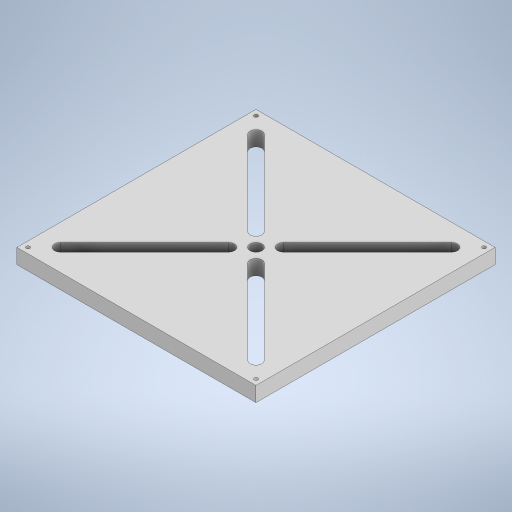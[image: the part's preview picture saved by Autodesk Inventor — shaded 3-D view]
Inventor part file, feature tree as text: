
AUTODESK INVENTOR PART (.ipt)
format: ipt  version: 2023 (Build 270158000, 158)  size: 280,576 bytes
history: native  units: in
note: dims shown in document units (in); Inventor stores cm internally (conversion verified against a paired STEP export)
features: sketch x3, extrude x2, projected_geometry x2
ambient origin geometry x8: Origin, YZ Plane, XZ Plane, XY Plane, X Axis, Y Axis, Z Axis, Center Point
bodies: Solid1 (feature_tree)
feature tree (7):
  extrude  "Extrusion1"  Depth=4.0in
  extrude  "Extrusion2"  Depth=0.25in TaperAngle=0.0deg
  sketch  "Sketch3"  dims[d20=0.0625in d21=0.0938in d22=0.0938in d23=0.7874in d25=3.8125in d26=0.7874in d28=3.8125in d31=0.25in d32=0.0in d33=0.201in d34=0.125in d35=0.2in d36=0.25in d37=1.5748in d39=360.0deg]
  sketch  "Sketch1"  dims[d0=4.0in d1=4.0in]
  sketch  "Sketch2"  dims[d2=0.1875in d11=0.25in d12=0.0in]
  projected_geometry  "Projected Loop1"
  projected_geometry  "Projected Loop2"
